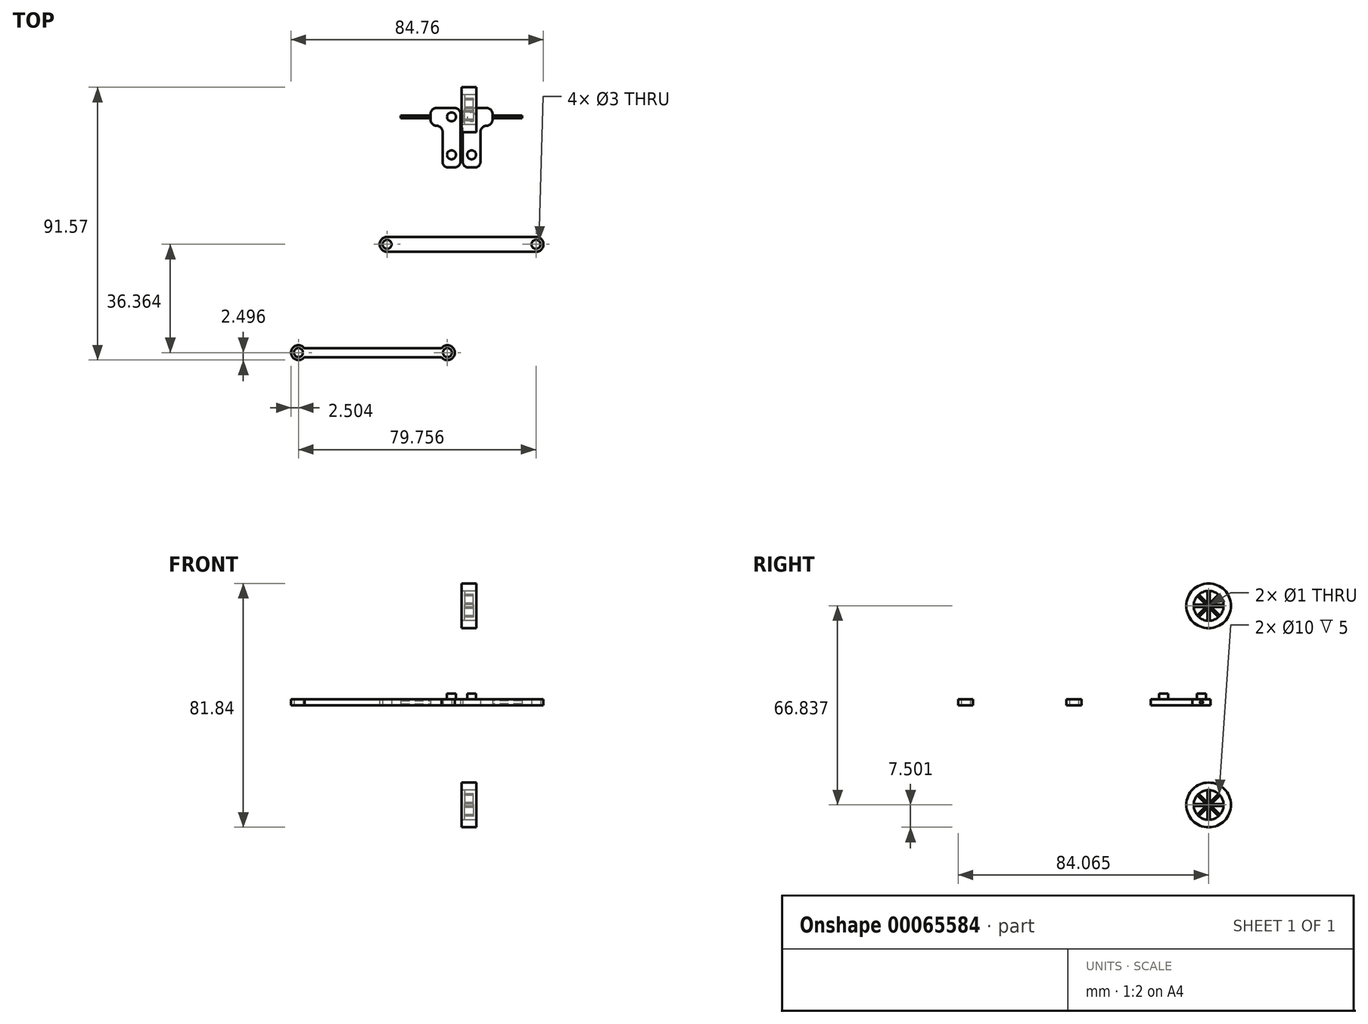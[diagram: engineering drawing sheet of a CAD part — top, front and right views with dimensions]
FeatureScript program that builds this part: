
annotation { "Feature Type Name" : "Feature", "Feature Type Description" : "" }
export const myFeature = defineFeature(function(context is Context, id is Id, definition is map)
    precondition{}
    {
        {
            var Q0;
            Q0=qCreatedBy(makeId("Top.planeOp"),FACE);
            var sketch = newSketch(context, id + "F0", { "sketchPlane" : qUnion([Q0])});
            skLineSegment(sketch, "E0", {"start": v(0, 0) * mm, "end": v(25, 0) * mm});
            skLineSegment(sketch, "E1", {"start": v(0, 0) * mm, "end": v(-25, 0) * mm});
            skLineSegment(sketch, "E2", {"start": v(-25, 5) * mm, "end": v(25, 5) * mm});
            skArc(sketch, "E3", {"start": v(-25, 5) * mm, "mid": v(-27.5, 2.5) * mm, "end": v(-25, 0) * mm});
            skArc(sketch, "E4", {"start": v(25, 0) * mm, "mid": v(27.5, 2.5) * mm, "end": v(25, 5) * mm});
            skCircle(sketch, "E5", {"center": v(-25, 2.5) * mm, "radius": 1.5 * mm});
            skCircle(sketch, "E6", {"center": v(25, 2.5) * mm, "radius": 1.5 * mm});
            skSolve(sketch);
        }
        {
            var Q0;
            Q0=makeQuery(id+"F0.imprint","IMPRINT",FACE,{"disambiguationData":[TD([[makeQuery(id+"F0.imprint","IMPRINT",EDGE,{"derivedFrom":sQuery(id+"F0.wireOp",EDGE,"E0")}),1.0]])]});
            extrude(context, id + "F1", {"entities" : qUnion([Q0]), "depth" : 2 * mm});
        }
        {
            var Q0;
            Q0=qCreatedBy(makeId("Top.planeOp"),FACE);
            var sketch = newSketch(context, id + "F2", { "sketchPlane" : qUnion([Q0])});
            skLineSegment(sketch, "E7", {"start": v(-0.38, 48.3) * mm, "end": v(-0.38, 28.3) * mm});
            skLineSegment(sketch, "E8", {"start": v(-0.38, 28.3) * mm, "end": v(-6.38, 28.3) * mm});
            skLineSegment(sketch, "E9", {"start": v(-6.38, 28.3) * mm, "end": v(-6.38, 42.3) * mm});
            skLineSegment(sketch, "E10", {"start": v(-6.38, 42.3) * mm, "end": v(-10.38, 42.3) * mm});
            skLineSegment(sketch, "E11", {"start": v(-10.38, 42.3) * mm, "end": v(-10.38, 48.3) * mm});
            skLineSegment(sketch, "E12", {"start": v(-10.38, 48.3) * mm, "end": v(-0.38, 48.3) * mm});
            skPoint(sketch, "E13", {"position": v(-3.38, 45.3) * mm});
            skPoint(sketch, "E13.positionSnap0", {"position": v(-10.38, 45.3) * mm});
            skPoint(sketch, "E13.positionSnap1", {"position": v(-3.38, 28.3) * mm});
            skPoint(sketch, "E14", {"position": v(-3.38, 32.55) * mm});
            skCircle(sketch, "E15", {"center": v(-3.38, 32.55) * mm, "radius": 1.5 * mm});
            skCircle(sketch, "E16", {"center": v(-3.38, 45.3) * mm, "radius": 1.5 * mm});
            skSolve(sketch);
        }
        {
            var Q0;
            Q0 = qSketchRegion(id + "F2", true);
            extrude(context, id + "F3", {"entities" : qUnion([Q0]), "depth" : 2 * mm});
        }
        {
            var Q0;
            Q0=qCreatedBy(makeId("Top.planeOp"),FACE);
            var sketch = newSketch(context, id + "F4", { "sketchPlane" : qUnion([Q0])});
            skCircle(sketch, "E17.0", {"center": v(-3.38, 45.3) * mm, "radius": 1.5 * mm, "construction": true});
            skCircle(sketch, "E18.0", {"center": v(-3.38, 32.55) * mm, "radius": 1.5 * mm});
            skCircle(sketch, "E19", {"center": v(-3.38, 45.3) * mm, "radius": 1.5 * mm});
            skSolve(sketch);
        }
        {
            var Q0;
            Q0 = qSketchRegion(id + "F4", true);
            extrude(context, id + "F5", {"entities" : qUnion([Q0]), "operationType" : NewBodyOperationType.ADD, "depth" : 4 * mm});
        }
        {
            var Q0;
            Q0=makeQuery(id+"F3.opExtrude","SWEPT_FACE",FACE,{"disambiguationData":[OSD([sQuery(id+"F2.wireOp",EDGE,"E11")])]});
            var sketch = newSketch(context, id + "F6", { "sketchPlane" : qUnion([Q0])});
            skLineSegment(sketch, "E20", {"start": v(-42.3, 1) * mm, "end": v(-48.3, 1) * mm, "construction": true});
            skLineSegment(sketch, "E21", {"start": v(-45.3, 2) * mm, "end": v(-45.3, 0) * mm, "construction": true});
            skPoint(sketch, "E22", {"position": v(-45.3, 1) * mm});
            skCircle(sketch, "E23", {"center": v(-45.3, 1) * mm, "radius": 0.5 * mm});
            skSolve(sketch);
        }
        {
            var Q0;
            Q0 = qSketchRegion(id + "F6", true);
            extrude(context, id + "F7", {"entities" : qUnion([Q0]), "operationType" : NewBodyOperationType.ADD, "depth" : 10 * mm});
        }
        {
            var Q0;
            Q0=makeQuery(id+"F3.opExtrude","SWEPT_BODY",BODY,{"disambiguationData":[OSD([sQuery(id+"F2.wireOp",EDGE,"E7"),sQuery(id+"F2.wireOp",EDGE,"E8"),sQuery(id+"F2.wireOp",EDGE,"E9"),sQuery(id+"F2.wireOp",EDGE,"E10"),sQuery(id+"F2.wireOp",EDGE,"E11"),sQuery(id+"F2.wireOp",EDGE,"E12"),sQuery(id+"F2.wireOp",EDGE,"E15"),sQuery(id+"F2.wireOp",EDGE,"E16")])]});
            var Q1;
            Q1=qCreatedBy(makeId("Right.planeOp"),FACE);
            mirror(context, id + "F8", {"entities" : qUnion([Q0]), "mirrorPlane" : qUnion([Q1])});
        }
        {
            var Q0;
            Q0=qCreatedBy(makeId("Top.planeOp"),FACE);
            var sketch = newSketch(context, id + "F9", { "sketchPlane" : qUnion([Q0])});
            skCircle(sketch, "E24", {"center": v(-54.76, -33.86) * mm, "radius": 2.5 * mm});
            skLineSegment(sketch, "E25", {"start": v(-54.76, -33.86) * mm, "end": v(-4.76, -33.86) * mm, "construction": true});
            skCircle(sketch, "E26", {"center": v(-4.76, -33.86) * mm, "radius": 2.5 * mm});
            skCircle(sketch, "E27", {"center": v(-54.76, -33.86) * mm, "radius": 1.5 * mm});
            skCircle(sketch, "E28", {"center": v(-4.76, -33.86) * mm, "radius": 1.5 * mm});
            skLineSegment(sketch, "E29", {"start": v(-54.76, -33.86) * mm, "end": v(-54.76, -32.36) * mm, "construction": true});
            skLineSegment(sketch, "E30", {"start": v(-54.76, -32.36) * mm, "end": v(-54.76, -35.36) * mm, "construction": true});
            skLineSegment(sketch, "E31", {"start": v(-54.76, -35.36) * mm, "end": v(-52.76, -35.36) * mm, "construction": true});
            skLineSegment(sketch, "E32", {"start": v(-54.76, -32.36) * mm, "end": v(-52.76, -32.36) * mm, "construction": true});
            skLineSegment(sketch, "E33", {"start": v(-4.76, -33.86) * mm, "end": v(-4.76, -32.36) * mm, "construction": true});
            skLineSegment(sketch, "E34", {"start": v(-4.76, -32.36) * mm, "end": v(-6.76, -32.36) * mm, "construction": true});
            skLineSegment(sketch, "E35", {"start": v(-4.76, -33.86) * mm, "end": v(-4.76, -35.36) * mm, "construction": true});
            skLineSegment(sketch, "E36", {"start": v(-4.76, -35.36) * mm, "end": v(-6.76, -35.36) * mm, "construction": true});
            skLineSegment(sketch, "E37", {"start": v(-52.76, -32.36) * mm, "end": v(-6.76, -32.36) * mm});
            skLineSegment(sketch, "E38", {"start": v(-6.76, -35.36) * mm, "end": v(-52.76, -35.36) * mm});
            skSolve(sketch);
        }
        {
            var Q0;
            Q0 = qSketchRegion(id + "F9", true);
            extrude(context, id + "F10", {"entities" : qUnion([Q0]), "depth" : 2 * mm});
        }
        {
            var Q0;
            Q0=qCreatedBy(makeId("Right.planeOp"),FACE);
            var sketch = newSketch(context, id + "F11", { "sketchPlane" : qUnion([Q0])});
            skCircle(sketch, "E39", {"center": v(47.7, -33.42) * mm, "radius": 0.5 * mm});
            skCircle(sketch, "E40", {"center": v(47.7, -33.42) * mm, "radius": 5 * mm});
            skLineSegment(sketch, "E41", {"start": v(47.7, -33.42) * mm, "end": v(52.7, -33.42) * mm});
            skLineSegment(sketch, "E42", {"start": v(47.7, -33.42) * mm, "end": v(47.7, -28.42) * mm});
            skLineSegment(sketch, "E43", {"start": v(47.7, -33.42) * mm, "end": v(42.7, -33.42) * mm});
            skLineSegment(sketch, "E44", {"start": v(47.7, -33.42) * mm, "end": v(47.7, -38.42) * mm});
            skCircle(sketch, "E45", {"center": v(47.7, -33.42) * mm, "radius": 7.5 * mm});
            skLineSegment(sketch, "E46", {"start": v(47.7, -33.42) * mm, "end": v(44.17, -29.88) * mm});
            skLineSegment(sketch, "E47", {"start": v(47.7, -33.42) * mm, "end": v(51.24, -29.88) * mm});
            skLineSegment(sketch, "E48", {"start": v(51.24, -29.88) * mm, "end": v(44.17, -29.88) * mm, "construction": true});
            skLineSegment(sketch, "E49", {"start": v(47.7, -33.42) * mm, "end": v(51.24, -36.95) * mm});
            skLineSegment(sketch, "E50", {"start": v(47.7, -33.42) * mm, "end": v(44.17, -36.95) * mm});
            skLineSegment(sketch, "E51", {"start": v(48.06, -33.07) * mm, "end": v(48.06, -28.43) * mm});
            skLineSegment(sketch, "E52", {"start": v(47.35, -33.07) * mm, "end": v(47.35, -28.43) * mm});
            skLineSegment(sketch, "E53", {"start": v(47.7, -32.92) * mm, "end": v(44.43, -29.64) * mm});
            skLineSegment(sketch, "E54", {"start": v(47.2, -33.42) * mm, "end": v(43.93, -30.14) * mm});
            skLineSegment(sketch, "E55", {"start": v(47.35, -33.07) * mm, "end": v(42.72, -33.07) * mm});
            skLineSegment(sketch, "E56", {"start": v(47.35, -33.77) * mm, "end": v(42.72, -33.77) * mm});
            skLineSegment(sketch, "E57", {"start": v(47.2, -33.42) * mm, "end": v(43.93, -36.7) * mm});
            skLineSegment(sketch, "E58", {"start": v(47.7, -33.92) * mm, "end": v(44.43, -37.2) * mm});
            skLineSegment(sketch, "E59", {"start": v(47.35, -33.77) * mm, "end": v(47.35, -38.4) * mm});
            skLineSegment(sketch, "E60", {"start": v(48.06, -33.77) * mm, "end": v(48.06, -38.4) * mm});
            skLineSegment(sketch, "E61", {"start": v(47.7, -33.92) * mm, "end": v(50.98, -37.2) * mm});
            skLineSegment(sketch, "E62", {"start": v(48.2, -33.42) * mm, "end": v(51.48, -36.7) * mm});
            skLineSegment(sketch, "E63", {"start": v(48.06, -33.77) * mm, "end": v(52.7, -33.77) * mm});
            skLineSegment(sketch, "E64", {"start": v(48.06, -33.07) * mm, "end": v(52.7, -33.07) * mm});
            skLineSegment(sketch, "E65", {"start": v(48.2, -33.42) * mm, "end": v(51.48, -30.14) * mm});
            skLineSegment(sketch, "E66", {"start": v(47.7, -32.92) * mm, "end": v(50.98, -29.64) * mm});
            skSolve(sketch);
        }
        {
            var Q0;
            Q0=makeQuery(id+"F11.imprint","IMPRINT",FACE,{"disambiguationData":[TD([[makeQuery(id+"F11.imprint","IMPRINT",EDGE,{"derivedFrom":sQuery(id+"F11.wireOp",EDGE,"E45")}),1.0]])]});
            var Q1;
            {var subQ0=sQuery(id+"F11.wireOp",EDGE,"E47");var subQ1=sQuery(id+"F11.wireOp",EDGE,"E40");var subQ2=makeQuery(id+"F11.imprint","INTERSECT",VERTEX,{"derivedFrom":[subQ1,subQ0]});Q1=makeQuery(id+"F11.imprint","IMPRINT",FACE,{"disambiguationData":[TD([[makeQuery(id+"F11.imprint","IMPRINT",EDGE,{"disambiguationData":[TD([[subQ2,-1.0]])],"derivedFrom":subQ1}),1.0]])]});}
            var Q2;
            {var subQ0=sQuery(id+"F11.wireOp",EDGE,"E47");var subQ1=sQuery(id+"F11.wireOp",EDGE,"E40");var subQ2=makeQuery(id+"F11.imprint","INTERSECT",VERTEX,{"derivedFrom":[subQ1,subQ0]});Q2=makeQuery(id+"F11.imprint","IMPRINT",FACE,{"disambiguationData":[TD([[makeQuery(id+"F11.imprint","IMPRINT",EDGE,{"disambiguationData":[TD([[subQ2,1.0]])],"derivedFrom":subQ1}),1.0]])]});}
            var Q3;
            {var subQ0=sQuery(id+"F11.wireOp",EDGE,"E42");var subQ1=sQuery(id+"F11.wireOp",EDGE,"E40");var subQ2=makeQuery(id+"F11.imprint","INTERSECT",VERTEX,{"derivedFrom":[subQ1,subQ0]});Q3=makeQuery(id+"F11.imprint","IMPRINT",FACE,{"disambiguationData":[TD([[makeQuery(id+"F11.imprint","IMPRINT",EDGE,{"disambiguationData":[TD([[subQ2,1.0]])],"derivedFrom":subQ1}),1.0]])]});}
            var Q4;
            {var subQ0=sQuery(id+"F11.wireOp",EDGE,"E42");var subQ1=sQuery(id+"F11.wireOp",EDGE,"E40");var subQ2=makeQuery(id+"F11.imprint","INTERSECT",VERTEX,{"derivedFrom":[subQ1,subQ0]});Q4=makeQuery(id+"F11.imprint","IMPRINT",FACE,{"disambiguationData":[TD([[makeQuery(id+"F11.imprint","IMPRINT",EDGE,{"disambiguationData":[TD([[subQ2,-1.0]])],"derivedFrom":subQ1}),1.0]])]});}
            var Q5;
            {var subQ0=sQuery(id+"F11.wireOp",EDGE,"E46");var subQ1=sQuery(id+"F11.wireOp",EDGE,"E40");var subQ2=makeQuery(id+"F11.imprint","INTERSECT",VERTEX,{"derivedFrom":[subQ1,subQ0]});Q5=makeQuery(id+"F11.imprint","IMPRINT",FACE,{"disambiguationData":[TD([[makeQuery(id+"F11.imprint","IMPRINT",EDGE,{"disambiguationData":[TD([[subQ2,1.0]])],"derivedFrom":subQ1}),1.0]])]});}
            var Q6;
            {var subQ0=sQuery(id+"F11.wireOp",EDGE,"E46");var subQ1=sQuery(id+"F11.wireOp",EDGE,"E40");var subQ2=makeQuery(id+"F11.imprint","INTERSECT",VERTEX,{"derivedFrom":[subQ1,subQ0]});Q6=makeQuery(id+"F11.imprint","IMPRINT",FACE,{"disambiguationData":[TD([[makeQuery(id+"F11.imprint","IMPRINT",EDGE,{"disambiguationData":[TD([[subQ2,-1.0]])],"derivedFrom":subQ1}),1.0]])]});}
            var Q7;
            {var subQ0=sQuery(id+"F11.wireOp",EDGE,"E43");var subQ1=sQuery(id+"F11.wireOp",EDGE,"E40");var subQ2=makeQuery(id+"F11.imprint","INTERSECT",VERTEX,{"derivedFrom":[subQ1,subQ0]});Q7=makeQuery(id+"F11.imprint","IMPRINT",FACE,{"disambiguationData":[TD([[makeQuery(id+"F11.imprint","IMPRINT",EDGE,{"disambiguationData":[TD([[subQ2,1.0]])],"derivedFrom":subQ1}),1.0]])]});}
            var Q8;
            {var subQ0=sQuery(id+"F11.wireOp",EDGE,"E43");var subQ1=sQuery(id+"F11.wireOp",EDGE,"E40");var subQ2=makeQuery(id+"F11.imprint","INTERSECT",VERTEX,{"derivedFrom":[subQ1,subQ0]});Q8=makeQuery(id+"F11.imprint","IMPRINT",FACE,{"disambiguationData":[TD([[makeQuery(id+"F11.imprint","IMPRINT",EDGE,{"disambiguationData":[TD([[subQ2,-1.0]])],"derivedFrom":subQ1}),1.0]])]});}
            var Q9;
            {var subQ0=sQuery(id+"F11.wireOp",EDGE,"E52");var subQ3=sQuery(id+"F11.wireOp",EDGE,"E53");var subQ5=makeQuery(id+"F11.imprint","INTERSECT",VERTEX,{"derivedFrom":[subQ0,subQ3]});Q9=makeQuery(id+"F11.imprint","IMPRINT",FACE,{"disambiguationData":[TD([[makeQuery(id+"F11.imprint","IMPRINT",EDGE,{"disambiguationData":[TD([[subQ5,1.0]])],"derivedFrom":subQ0}),-1.0]])]});}
            var Q10;
            {var subQ0=sQuery(id+"F11.wireOp",EDGE,"E51");var subQ3=sQuery(id+"F11.wireOp",EDGE,"E66");var subQ5=makeQuery(id+"F11.imprint","INTERSECT",VERTEX,{"derivedFrom":[subQ0,subQ3]});Q10=makeQuery(id+"F11.imprint","IMPRINT",FACE,{"disambiguationData":[TD([[makeQuery(id+"F11.imprint","IMPRINT",EDGE,{"disambiguationData":[TD([[subQ5,1.0]])],"derivedFrom":subQ0}),1.0]])]});}
            var Q11;
            {var subQ0=sQuery(id+"F11.wireOp",EDGE,"E64");var subQ3=sQuery(id+"F11.wireOp",EDGE,"E65");var subQ5=makeQuery(id+"F11.imprint","INTERSECT",VERTEX,{"derivedFrom":[subQ0,subQ3]});Q11=makeQuery(id+"F11.imprint","IMPRINT",FACE,{"disambiguationData":[TD([[makeQuery(id+"F11.imprint","IMPRINT",EDGE,{"disambiguationData":[TD([[subQ5,1.0]])],"derivedFrom":subQ0}),-1.0]])]});}
            var Q12;
            {var subQ0=sQuery(id+"F11.wireOp",EDGE,"E63");var subQ3=sQuery(id+"F11.wireOp",EDGE,"E62");var subQ5=makeQuery(id+"F11.imprint","INTERSECT",VERTEX,{"derivedFrom":[subQ3,subQ0]});Q12=makeQuery(id+"F11.imprint","IMPRINT",FACE,{"disambiguationData":[TD([[makeQuery(id+"F11.imprint","IMPRINT",EDGE,{"disambiguationData":[TD([[subQ5,1.0]])],"derivedFrom":subQ3}),-1.0]])]});}
            var Q13;
            {var subQ0=sQuery(id+"F11.wireOp",EDGE,"E61");var subQ3=sQuery(id+"F11.wireOp",EDGE,"E60");var subQ5=makeQuery(id+"F11.imprint","INTERSECT",VERTEX,{"derivedFrom":[subQ3,subQ0]});Q13=makeQuery(id+"F11.imprint","IMPRINT",FACE,{"disambiguationData":[TD([[makeQuery(id+"F11.imprint","IMPRINT",EDGE,{"disambiguationData":[TD([[subQ5,1.0]])],"derivedFrom":subQ3}),-1.0]])]});}
            var Q14;
            {var subQ0=sQuery(id+"F11.wireOp",EDGE,"E59");var subQ3=sQuery(id+"F11.wireOp",EDGE,"E58");var subQ5=makeQuery(id+"F11.imprint","INTERSECT",VERTEX,{"derivedFrom":[subQ3,subQ0]});Q14=makeQuery(id+"F11.imprint","IMPRINT",FACE,{"disambiguationData":[TD([[makeQuery(id+"F11.imprint","IMPRINT",EDGE,{"disambiguationData":[TD([[subQ5,1.0]])],"derivedFrom":subQ3}),-1.0]])]});}
            var Q15;
            {var subQ0=sQuery(id+"F11.wireOp",EDGE,"E57");var subQ3=sQuery(id+"F11.wireOp",EDGE,"E56");var subQ5=makeQuery(id+"F11.imprint","INTERSECT",VERTEX,{"derivedFrom":[subQ3,subQ0]});Q15=makeQuery(id+"F11.imprint","IMPRINT",FACE,{"disambiguationData":[TD([[makeQuery(id+"F11.imprint","IMPRINT",EDGE,{"disambiguationData":[TD([[subQ5,1.0]])],"derivedFrom":subQ3}),-1.0]])]});}
            var Q16;
            {var subQ0=sQuery(id+"F11.wireOp",EDGE,"E55");var subQ3=sQuery(id+"F11.wireOp",EDGE,"E54");var subQ5=makeQuery(id+"F11.imprint","INTERSECT",VERTEX,{"derivedFrom":[subQ3,subQ0]});Q16=makeQuery(id+"F11.imprint","IMPRINT",FACE,{"disambiguationData":[TD([[makeQuery(id+"F11.imprint","IMPRINT",EDGE,{"disambiguationData":[TD([[subQ5,1.0]])],"derivedFrom":subQ3}),-1.0]])]});}
            var Q17;
            {var subQ0=sQuery(id+"F11.wireOp",EDGE,"E50");var subQ1=sQuery(id+"F11.wireOp",EDGE,"E40");var subQ2=makeQuery(id+"F11.imprint","INTERSECT",VERTEX,{"derivedFrom":[subQ1,subQ0]});Q17=makeQuery(id+"F11.imprint","IMPRINT",FACE,{"disambiguationData":[TD([[makeQuery(id+"F11.imprint","IMPRINT",EDGE,{"disambiguationData":[TD([[subQ2,1.0]])],"derivedFrom":subQ1}),1.0]])]});}
            var Q18;
            {var subQ0=sQuery(id+"F11.wireOp",EDGE,"E50");var subQ1=sQuery(id+"F11.wireOp",EDGE,"E40");var subQ2=makeQuery(id+"F11.imprint","INTERSECT",VERTEX,{"derivedFrom":[subQ1,subQ0]});Q18=makeQuery(id+"F11.imprint","IMPRINT",FACE,{"disambiguationData":[TD([[makeQuery(id+"F11.imprint","IMPRINT",EDGE,{"disambiguationData":[TD([[subQ2,-1.0]])],"derivedFrom":subQ1}),1.0]])]});}
            var Q19;
            {var subQ0=sQuery(id+"F11.wireOp",EDGE,"E44");var subQ1=sQuery(id+"F11.wireOp",EDGE,"E40");var subQ2=makeQuery(id+"F11.imprint","INTERSECT",VERTEX,{"derivedFrom":[subQ1,subQ0]});Q19=makeQuery(id+"F11.imprint","IMPRINT",FACE,{"disambiguationData":[TD([[makeQuery(id+"F11.imprint","IMPRINT",EDGE,{"disambiguationData":[TD([[subQ2,1.0]])],"derivedFrom":subQ1}),1.0]])]});}
            var Q20;
            {var subQ0=sQuery(id+"F11.wireOp",EDGE,"E44");var subQ1=sQuery(id+"F11.wireOp",EDGE,"E40");var subQ2=makeQuery(id+"F11.imprint","INTERSECT",VERTEX,{"derivedFrom":[subQ1,subQ0]});Q20=makeQuery(id+"F11.imprint","IMPRINT",FACE,{"disambiguationData":[TD([[makeQuery(id+"F11.imprint","IMPRINT",EDGE,{"disambiguationData":[TD([[subQ2,-1.0]])],"derivedFrom":subQ1}),1.0]])]});}
            var Q21;
            {var subQ0=sQuery(id+"F11.wireOp",EDGE,"E49");var subQ1=sQuery(id+"F11.wireOp",EDGE,"E40");var subQ2=makeQuery(id+"F11.imprint","INTERSECT",VERTEX,{"derivedFrom":[subQ1,subQ0]});Q21=makeQuery(id+"F11.imprint","IMPRINT",FACE,{"disambiguationData":[TD([[makeQuery(id+"F11.imprint","IMPRINT",EDGE,{"disambiguationData":[TD([[subQ2,1.0]])],"derivedFrom":subQ1}),1.0]])]});}
            var Q22;
            {var subQ0=sQuery(id+"F11.wireOp",EDGE,"E49");var subQ1=sQuery(id+"F11.wireOp",EDGE,"E40");var subQ2=makeQuery(id+"F11.imprint","INTERSECT",VERTEX,{"derivedFrom":[subQ1,subQ0]});Q22=makeQuery(id+"F11.imprint","IMPRINT",FACE,{"disambiguationData":[TD([[makeQuery(id+"F11.imprint","IMPRINT",EDGE,{"disambiguationData":[TD([[subQ2,-1.0]])],"derivedFrom":subQ1}),1.0]])]});}
            var Q23;
            {var subQ0=sQuery(id+"F11.wireOp",EDGE,"E41");var subQ1=sQuery(id+"F11.wireOp",EDGE,"E40");var subQ2=makeQuery(id+"F11.imprint","INTERSECT",VERTEX,{"derivedFrom":[subQ1,subQ0]});Q23=makeQuery(id+"F11.imprint","IMPRINT",FACE,{"disambiguationData":[TD([[makeQuery(id+"F11.imprint","IMPRINT",EDGE,{"disambiguationData":[TD([[subQ2,1.0]])],"derivedFrom":subQ1}),1.0]])]});}
            var Q24;
            {var subQ0=sQuery(id+"F11.wireOp",EDGE,"E41");var subQ1=sQuery(id+"F11.wireOp",EDGE,"E40");var subQ2=makeQuery(id+"F11.imprint","INTERSECT",VERTEX,{"derivedFrom":[subQ1,subQ0]});Q24=makeQuery(id+"F11.imprint","IMPRINT",FACE,{"disambiguationData":[TD([[makeQuery(id+"F11.imprint","IMPRINT",EDGE,{"disambiguationData":[TD([[subQ2,-1.0]])],"derivedFrom":subQ1}),1.0]])]});}
            extrude(context, id + "F12", {"entities" : qUnion([Q0, Q1, Q2, Q3, Q4, Q5, Q6, Q7, Q8, Q9, Q10, Q11, Q12, Q13, Q14, Q15, Q16, Q17, Q18, Q19, Q20, Q21, Q22, Q23, Q24]), "depth" : 5 * mm});
        }
        {
            var Q0;
            Q0=makeQuery(id+"F12.opExtrude","CAP_FACE",FACE,{"disambiguationData":[OSD([sQuery(id+"F11.wireOp",EDGE,"E39"),sQuery(id+"F11.wireOp",EDGE,"E40"),sQuery(id+"F11.wireOp",EDGE,"E45"),sQuery(id+"F11.wireOp",EDGE,"E51"),sQuery(id+"F11.wireOp",EDGE,"E52"),sQuery(id+"F11.wireOp",EDGE,"E53"),sQuery(id+"F11.wireOp",EDGE,"E54"),sQuery(id+"F11.wireOp",EDGE,"E55"),sQuery(id+"F11.wireOp",EDGE,"E56"),sQuery(id+"F11.wireOp",EDGE,"E57"),sQuery(id+"F11.wireOp",EDGE,"E58"),sQuery(id+"F11.wireOp",EDGE,"E59"),sQuery(id+"F11.wireOp",EDGE,"E60"),sQuery(id+"F11.wireOp",EDGE,"E61"),sQuery(id+"F11.wireOp",EDGE,"E62"),sQuery(id+"F11.wireOp",EDGE,"E63"),sQuery(id+"F11.wireOp",EDGE,"E64"),sQuery(id+"F11.wireOp",EDGE,"E65"),sQuery(id+"F11.wireOp",EDGE,"E66")])],"isStart":true});
            var sketch = newSketch(context, id + "F13", { "sketchPlane" : qUnion([Q0])});
            skArc(sketch, "E67.0", {"start": v(-50.98, -29.64) * mm, "mid": v(-49.62, -28.8) * mm, "end": v(-48.06, -28.43) * mm});
            skArc(sketch, "E68.0", {"start": v(-47.35, -28.43) * mm, "mid": v(-45.8, -28.8) * mm, "end": v(-44.43, -29.64) * mm});
            skArc(sketch, "E69.0", {"start": v(-43.93, -30.14) * mm, "mid": v(-43.09, -31.5) * mm, "end": v(-42.72, -33.07) * mm});
            skArc(sketch, "E70.0", {"start": v(-42.72, -33.77) * mm, "mid": v(-43.09, -35.33) * mm, "end": v(-43.93, -36.7) * mm});
            skArc(sketch, "E71.0", {"start": v(-44.43, -37.2) * mm, "mid": v(-45.8, -38.04) * mm, "end": v(-47.35, -38.4) * mm});
            skArc(sketch, "E72.0", {"start": v(-48.06, -38.4) * mm, "mid": v(-49.62, -38.04) * mm, "end": v(-50.98, -37.2) * mm});
            skArc(sketch, "E73.0", {"start": v(-51.48, -36.7) * mm, "mid": v(-52.32, -35.33) * mm, "end": v(-52.7, -33.77) * mm});
            skArc(sketch, "E74.0", {"start": v(-52.7, -33.07) * mm, "mid": v(-52.32, -31.5) * mm, "end": v(-51.48, -30.14) * mm});
            skCircle(sketch, "E75.0", {"center": v(-47.7, -33.42) * mm, "radius": 0.5 * mm});
            skLineSegment(sketch, "E76.0", {"start": v(-47.35, -32.57) * mm, "end": v(-44.43, -29.64) * mm});
            skLineSegment(sketch, "E77.0", {"start": v(-47.35, -32.57) * mm, "end": v(-47.35, -28.43) * mm});
            skLineSegment(sketch, "E78.0", {"start": v(-48.06, -32.57) * mm, "end": v(-48.06, -28.43) * mm});
            skLineSegment(sketch, "E79.0", {"start": v(-48.06, -32.57) * mm, "end": v(-50.98, -29.64) * mm});
            skLineSegment(sketch, "E80.0", {"start": v(-48.56, -33.07) * mm, "end": v(-51.48, -30.14) * mm});
            skLineSegment(sketch, "E81.0", {"start": v(-48.56, -33.07) * mm, "end": v(-52.7, -33.07) * mm});
            skLineSegment(sketch, "E82.0", {"start": v(-48.56, -33.77) * mm, "end": v(-51.48, -36.7) * mm});
            skLineSegment(sketch, "E83.0", {"start": v(-48.56, -33.77) * mm, "end": v(-52.7, -33.77) * mm});
            skLineSegment(sketch, "E84.0", {"start": v(-48.06, -34.27) * mm, "end": v(-50.98, -37.2) * mm});
            skLineSegment(sketch, "E85.0", {"start": v(-47.35, -34.27) * mm, "end": v(-44.43, -37.2) * mm});
            skLineSegment(sketch, "E86.0", {"start": v(-47.35, -34.27) * mm, "end": v(-47.35, -38.4) * mm});
            skLineSegment(sketch, "E87.0", {"start": v(-46.85, -33.77) * mm, "end": v(-43.93, -36.7) * mm});
            skLineSegment(sketch, "E88.0", {"start": v(-46.85, -33.77) * mm, "end": v(-42.72, -33.77) * mm});
            skLineSegment(sketch, "E89.0", {"start": v(-46.85, -33.07) * mm, "end": v(-42.72, -33.07) * mm});
            skLineSegment(sketch, "E90.0", {"start": v(-46.85, -33.07) * mm, "end": v(-43.93, -30.14) * mm});
            skCircle(sketch, "E91", {"center": v(-47.7, -33.42) * mm, "radius": 5 * mm});
            skSolve(sketch);
        }
        {
            var Q0;
            Q0 = qSketchRegion(id + "F13", true);
            var Q1;
            Q1=makeQuery(id+"F13.imprint","IMPRINT",FACE,{"disambiguationData":[TD([[makeQuery(id+"F13.imprint","IMPRINT",EDGE,{"derivedFrom":sQuery(id+"F13.wireOp",EDGE,"E75.0")}),1.0]])]});
            extrude(context, id + "F14", {"entities" : qUnion([Q0, Q1]), "operationType" : NewBodyOperationType.REMOVE, "oppositeDirection" : true, "depth" : 1 * mm});
        }
        {
            var Q0;
            Q0=makeQuery(id+"F12.opExtrude","CAP_FACE",FACE,{"disambiguationData":[OSD([sQuery(id+"F11.wireOp",EDGE,"E39"),sQuery(id+"F11.wireOp",EDGE,"E40"),sQuery(id+"F11.wireOp",EDGE,"E45"),sQuery(id+"F11.wireOp",EDGE,"E51"),sQuery(id+"F11.wireOp",EDGE,"E52"),sQuery(id+"F11.wireOp",EDGE,"E53"),sQuery(id+"F11.wireOp",EDGE,"E54"),sQuery(id+"F11.wireOp",EDGE,"E55"),sQuery(id+"F11.wireOp",EDGE,"E56"),sQuery(id+"F11.wireOp",EDGE,"E57"),sQuery(id+"F11.wireOp",EDGE,"E58"),sQuery(id+"F11.wireOp",EDGE,"E59"),sQuery(id+"F11.wireOp",EDGE,"E60"),sQuery(id+"F11.wireOp",EDGE,"E61"),sQuery(id+"F11.wireOp",EDGE,"E62"),sQuery(id+"F11.wireOp",EDGE,"E63"),sQuery(id+"F11.wireOp",EDGE,"E64"),sQuery(id+"F11.wireOp",EDGE,"E65"),sQuery(id+"F11.wireOp",EDGE,"E66")])],"isStart":false});
            var sketch = newSketch(context, id + "F15", { "sketchPlane" : qUnion([Q0])});
            skArc(sketch, "E92.0", {"start": v(50.98, -29.64) * mm, "mid": v(49.62, -28.8) * mm, "end": v(48.06, -28.43) * mm});
            skCircle(sketch, "E93", {"center": v(47.7, -33.42) * mm, "radius": 5 * mm});
            skSolve(sketch);
        }
        {
            var Q0;
            Q0=makeQuery(id+"F15.imprint","IMPRINT",FACE,{"disambiguationData":[TD([[makeQuery(id+"F15.imprint","IMPRINT",EDGE,{"derivedFrom":makeQuery(id+"F12.opExtrude","CAP_EDGE",EDGE,{"disambiguationData":[OSD([sQuery(id+"F11.wireOp",EDGE,"E39")])],"isStart":false})}),-1.0]])]});
            extrude(context, id + "F16", {"entities" : qUnion([Q0]), "operationType" : NewBodyOperationType.REMOVE, "oppositeDirection" : true, "depth" : 1 * mm});
        }
        {
            var Q0;
            Q0=makeQuery(id+"F12.opExtrude","SWEPT_BODY",BODY,{"disambiguationData":[OSD([sQuery(id+"F11.wireOp",EDGE,"E39"),sQuery(id+"F11.wireOp",EDGE,"E40"),sQuery(id+"F11.wireOp",EDGE,"E45"),sQuery(id+"F11.wireOp",EDGE,"E51"),sQuery(id+"F11.wireOp",EDGE,"E52"),sQuery(id+"F11.wireOp",EDGE,"E53"),sQuery(id+"F11.wireOp",EDGE,"E54"),sQuery(id+"F11.wireOp",EDGE,"E55"),sQuery(id+"F11.wireOp",EDGE,"E56"),sQuery(id+"F11.wireOp",EDGE,"E57"),sQuery(id+"F11.wireOp",EDGE,"E58"),sQuery(id+"F11.wireOp",EDGE,"E59"),sQuery(id+"F11.wireOp",EDGE,"E60"),sQuery(id+"F11.wireOp",EDGE,"E61"),sQuery(id+"F11.wireOp",EDGE,"E62"),sQuery(id+"F11.wireOp",EDGE,"E63"),sQuery(id+"F11.wireOp",EDGE,"E64"),sQuery(id+"F11.wireOp",EDGE,"E65"),sQuery(id+"F11.wireOp",EDGE,"E66")])]});
            var Q1;
            Q1=qCreatedBy(makeId("Top.planeOp"),FACE);
            mirror(context, id + "F17", {"entities" : qUnion([Q0]), "mirrorPlane" : qUnion([Q1])});
        }
        {
            var Q0;
            Q0=makeQuery(id+"F3.opExtrude","SWEPT_EDGE",EDGE,{"disambiguationData":[OSD([sQuery(id+"F2.wireOp",EDGE,"E11"),sQuery(id+"F2.wireOp",EDGE,"E12")])]});
            fillet(context, id + "F18", {"entities" : qUnion([Q0]), "radius" : 2 * mm, "tangentPropagation" : true, "allowEdgeOverflow" : false});
        }
        {
            var Q0;
            Q0=makeQuery(id+"F3.opExtrude","SWEPT_EDGE",EDGE,{"disambiguationData":[OSD([sQuery(id+"F2.wireOp",EDGE,"E10"),sQuery(id+"F2.wireOp",EDGE,"E11")])]});
            var Q1;
            Q1=makeQuery(id+"F3.opExtrude","SWEPT_EDGE",EDGE,{"disambiguationData":[OSD([sQuery(id+"F2.wireOp",EDGE,"E9"),sQuery(id+"F2.wireOp",EDGE,"E10")])]});
            var Q2;
            Q2=makeQuery(id+"F3.opExtrude","SWEPT_EDGE",EDGE,{"disambiguationData":[OSD([sQuery(id+"F2.wireOp",EDGE,"E8"),sQuery(id+"F2.wireOp",EDGE,"E9")])]});
            var Q3;
            Q3=makeQuery(id+"F3.opExtrude","SWEPT_EDGE",EDGE,{"disambiguationData":[OSD([sQuery(id+"F2.wireOp",EDGE,"E7"),sQuery(id+"F2.wireOp",EDGE,"E8")])]});
            var Q4;
            Q4=makeQuery(id+"F3.opExtrude","SWEPT_EDGE",EDGE,{"disambiguationData":[OSD([sQuery(id+"F2.wireOp",EDGE,"E7"),sQuery(id+"F2.wireOp",EDGE,"E12")])]});
            fillet(context, id + "F19", {"entities" : qUnion([Q0, Q1, Q2, Q3, Q4]), "radius" : 2 * mm, "tangentPropagation" : true, "allowEdgeOverflow" : false});
        }
        {
            var Q0;
            Q0=makeQuery(id+"F8.opPattern","COPY",EDGE,{"derivedFrom":makeQuery(id+"F3.opExtrude","SWEPT_EDGE",EDGE,{"disambiguationData":[OSD([sQuery(id+"F2.wireOp",EDGE,"E7"),sQuery(id+"F2.wireOp",EDGE,"E12")])]}),"instanceName":"1"});
            var Q1;
            Q1=makeQuery(id+"F8.opPattern","COPY",EDGE,{"derivedFrom":makeQuery(id+"F3.opExtrude","SWEPT_EDGE",EDGE,{"disambiguationData":[OSD([sQuery(id+"F2.wireOp",EDGE,"E11"),sQuery(id+"F2.wireOp",EDGE,"E12")])]}),"instanceName":"1"});
            var Q2;
            Q2=makeQuery(id+"F8.opPattern","COPY",EDGE,{"derivedFrom":makeQuery(id+"F3.opExtrude","SWEPT_EDGE",EDGE,{"disambiguationData":[OSD([sQuery(id+"F2.wireOp",EDGE,"E10"),sQuery(id+"F2.wireOp",EDGE,"E11")])]}),"instanceName":"1"});
            var Q3;
            Q3=makeQuery(id+"F8.opPattern","COPY",EDGE,{"derivedFrom":makeQuery(id+"F3.opExtrude","SWEPT_EDGE",EDGE,{"disambiguationData":[OSD([sQuery(id+"F2.wireOp",EDGE,"E8"),sQuery(id+"F2.wireOp",EDGE,"E9")])]}),"instanceName":"1"});
            var Q4;
            Q4=makeQuery(id+"F8.opPattern","COPY",EDGE,{"derivedFrom":makeQuery(id+"F3.opExtrude","SWEPT_EDGE",EDGE,{"disambiguationData":[OSD([sQuery(id+"F2.wireOp",EDGE,"E7"),sQuery(id+"F2.wireOp",EDGE,"E8")])]}),"instanceName":"1"});
            var Q5;
            Q5=makeQuery(id+"F8.opPattern","COPY",EDGE,{"derivedFrom":makeQuery(id+"F3.opExtrude","SWEPT_EDGE",EDGE,{"disambiguationData":[OSD([sQuery(id+"F2.wireOp",EDGE,"E9"),sQuery(id+"F2.wireOp",EDGE,"E10")])]}),"instanceName":"1"});
            fillet(context, id + "F20", {"entities" : qUnion([Q0, Q1, Q2, Q3, Q4, Q5]), "radius" : 2 * mm, "tangentPropagation" : true, "allowEdgeOverflow" : false});
        }
    });
